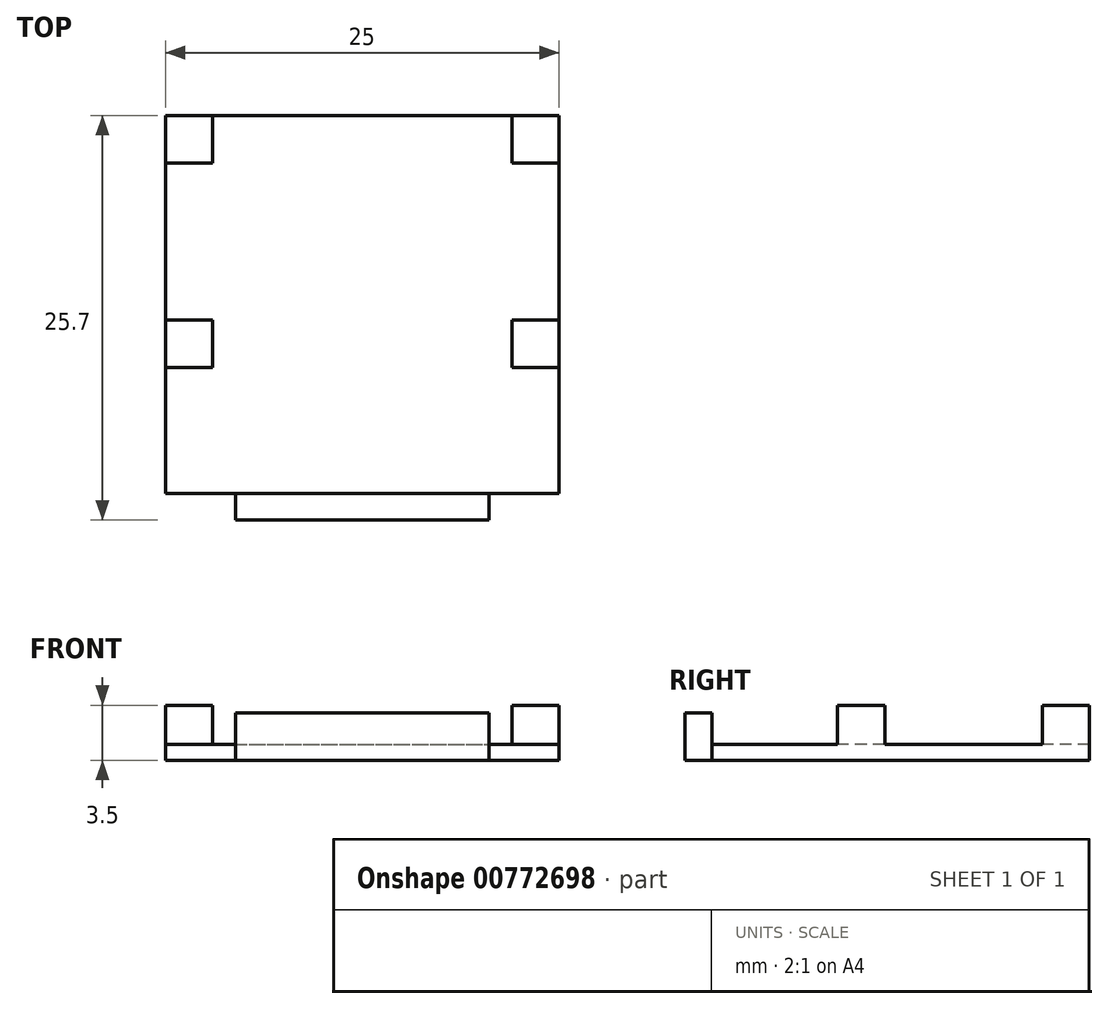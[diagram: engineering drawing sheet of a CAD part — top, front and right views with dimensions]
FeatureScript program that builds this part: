
annotation { "Feature Type Name" : "Feature", "Feature Type Description" : "" }
export const myFeature = defineFeature(function(context is Context, id is Id, definition is map)
    precondition{}
    {
        {
            var Q0;
            Q0=qCreatedBy(makeId("Top.planeOp"),FACE);
            var sketch = newSketch(context, id + "F0", { "sketchPlane" : qUnion([Q0])});
            skLineSegment(sketch, "E0.bottom", {"start": v(-12.5, 12) * mm, "end": v(12.5, 12) * mm});
            skLineSegment(sketch, "E0.top", {"start": v(-12.5, -12) * mm, "end": v(-8.05, -12) * mm});
            skLineSegment(sketch, "E0.left", {"start": v(-12.5, 12) * mm, "end": v(-12.5, -12) * mm});
            skLineSegment(sketch, "E0.right", {"start": v(12.5, 12) * mm, "end": v(12.5, -12) * mm});
            skLineSegment(sketch, "E1", {"start": v(8.05, -12) * mm, "end": v(8.05, -13.7) * mm});
            skLineSegment(sketch, "E2", {"start": v(-8.05, -12) * mm, "end": v(-8.05, -13.7) * mm});
            skLineSegment(sketch, "E3", {"start": v(-8.05, -13.7) * mm, "end": v(8.05, -13.7) * mm});
            skLineSegment(sketch, "E4.trimOffspring", {"start": v(8.05, -12) * mm, "end": v(12.5, -12) * mm});
            skLineSegment(sketch, "E5", {"start": v(-12.5, 9) * mm, "end": v(-9.5, 9) * mm});
            skLineSegment(sketch, "E6", {"start": v(-9.5, 9) * mm, "end": v(-9.5, 12) * mm});
            skLineSegment(sketch, "E7", {"start": v(9.5, 12) * mm, "end": v(9.5, 9) * mm});
            skLineSegment(sketch, "E8", {"start": v(9.5, 9) * mm, "end": v(12.5, 9) * mm});
            skLineSegment(sketch, "E9", {"start": v(-12.5, -1) * mm, "end": v(-9.5, -1) * mm});
            skLineSegment(sketch, "E10", {"start": v(-9.5, -1) * mm, "end": v(-9.5, -4) * mm});
            skLineSegment(sketch, "E11", {"start": v(-9.5, -4) * mm, "end": v(-12.5, -4) * mm});
            skLineSegment(sketch, "E12", {"start": v(12.5, -1) * mm, "end": v(9.5, -1) * mm});
            skLineSegment(sketch, "E13", {"start": v(9.5, -1) * mm, "end": v(9.5, -4) * mm});
            skLineSegment(sketch, "E14", {"start": v(9.5, -4) * mm, "end": v(12.5, -4) * mm});
            skLineSegment(sketch, "E15", {"start": v(-8.05, -12) * mm, "end": v(8.05, -12) * mm});
            skSolve(sketch);
        }
        {
            var Q0;
            {var subQ4=sQuery(id+"F0.wireOp",EDGE,"E5");Q0=makeQuery(id+"F0.imprint","IMPRINT",FACE,{"disambiguationData":[TD([[makeQuery(id+"F0.imprint","IMPRINT",EDGE,{"derivedFrom":subQ4}),1.0]])]});}
            var Q1;
            {var subQ8=sQuery(id+"F0.wireOp",EDGE,"E0.top");Q1=makeQuery(id+"F0.imprint","IMPRINT",FACE,{"disambiguationData":[TD([[makeQuery(id+"F0.imprint","IMPRINT",EDGE,{"derivedFrom":subQ8}),1.0]])]});}
            var Q2;
            {var subQ3=sQuery(id+"F0.wireOp",EDGE,"E7");Q2=makeQuery(id+"F0.imprint","IMPRINT",FACE,{"disambiguationData":[TD([[makeQuery(id+"F0.imprint","IMPRINT",EDGE,{"derivedFrom":subQ3}),1.0]])]});}
            var Q3;
            {var subQ0=sQuery(id+"F0.wireOp",EDGE,"E12");Q3=makeQuery(id+"F0.imprint","IMPRINT",FACE,{"disambiguationData":[TD([[makeQuery(id+"F0.imprint","IMPRINT",EDGE,{"derivedFrom":subQ0}),1.0]])]});}
            var Q4;
            {var subQ0=sQuery(id+"F0.wireOp",EDGE,"E9");Q4=makeQuery(id+"F0.imprint","IMPRINT",FACE,{"disambiguationData":[TD([[makeQuery(id+"F0.imprint","IMPRINT",EDGE,{"derivedFrom":subQ0}),-1.0]])]});}
            var Q5;
            Q5=makeQuery(id+"F0.imprint","IMPRINT",FACE,{"disambiguationData":[TD([[makeQuery(id+"F0.imprint","IMPRINT",EDGE,{"derivedFrom":sQuery(id+"F0.wireOp",EDGE,"E1")}),-1.0]])]});
            extrude(context, id + "F1", {"entities" : qUnion([Q0, Q1, Q2, Q3, Q4, Q5]), "oppositeDirection" : true, "depth" : 1 * mm, "offsetDistance" : 25 * mm});
        }
        {
            var Q0;
            {var subQ4=sQuery(id+"F0.wireOp",EDGE,"E5");Q0=makeQuery(id+"F0.imprint","IMPRINT",FACE,{"disambiguationData":[TD([[makeQuery(id+"F0.imprint","IMPRINT",EDGE,{"derivedFrom":subQ4}),1.0]])]});}
            var Q1;
            {var subQ3=sQuery(id+"F0.wireOp",EDGE,"E7");Q1=makeQuery(id+"F0.imprint","IMPRINT",FACE,{"disambiguationData":[TD([[makeQuery(id+"F0.imprint","IMPRINT",EDGE,{"derivedFrom":subQ3}),1.0]])]});}
            var Q2;
            {var subQ0=sQuery(id+"F0.wireOp",EDGE,"E9");Q2=makeQuery(id+"F0.imprint","IMPRINT",FACE,{"disambiguationData":[TD([[makeQuery(id+"F0.imprint","IMPRINT",EDGE,{"derivedFrom":subQ0}),-1.0]])]});}
            var Q3;
            {var subQ0=sQuery(id+"F0.wireOp",EDGE,"E12");Q3=makeQuery(id+"F0.imprint","IMPRINT",FACE,{"disambiguationData":[TD([[makeQuery(id+"F0.imprint","IMPRINT",EDGE,{"derivedFrom":subQ0}),1.0]])]});}
            extrude(context, id + "F2", {"entities" : qUnion([Q0, Q1, Q2, Q3]), "operationType" : NewBodyOperationType.ADD, "depth" : 2.5 * mm, "offsetDistance" : 25 * mm});
        }
        {
            var Q0;
            Q0=makeQuery(id+"F0.imprint","IMPRINT",FACE,{"disambiguationData":[TD([[makeQuery(id+"F0.imprint","IMPRINT",EDGE,{"derivedFrom":sQuery(id+"F0.wireOp",EDGE,"E1")}),-1.0]])]});
            extrude(context, id + "F3", {"entities" : qUnion([Q0]), "operationType" : NewBodyOperationType.ADD, "depth" : 2 * mm, "offsetDistance" : 25 * mm});
        }
    });
